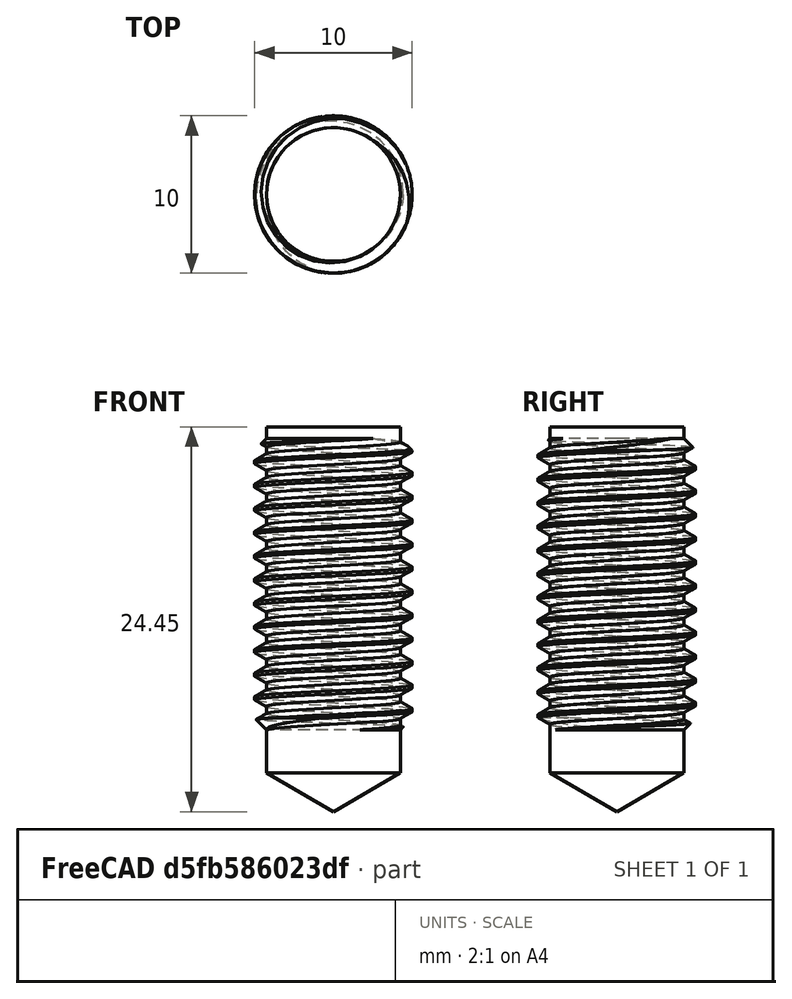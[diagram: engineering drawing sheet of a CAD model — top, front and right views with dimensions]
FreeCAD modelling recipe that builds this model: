
FCSTD DOCUMENT  (FreeCAD 0.22R36731 (Git))
Label: ThreadedHoll
License: All rights reserved
objects: Part::FeaturePython×1, Part::Cylinder×1, Part::Cone×1, Part::MultiFuse×1, Spreadsheet::Sheet×1, App::Part×1
note: 4 computed .brp shape members not serialized (recipe doc carries the construction recipe); baked Part::Feature solids carry a one-line shape summary decoded from their .brp

FEATURE [Part::FeaturePython] ThreadedRod  label="M10x20-ThreadedRod"  # Fasteners workbench fastener (typed FeaturePython)
  diameter = 10
  diameterCustom = 6
  invert = false
  leftHanded = false
  length = 20
  matchOuter = false
  offset = 0
  pitchCustom = 1
  thread = true
  type = 4
FEATURE [Part::Cylinder] Cylinder  label="円柱"
  Angle = 360
  AttacherType = Attacher::AttachEngine3D
  FirstAngle = 0
  Height = 22
  Placement = pos=(0,0,0) rot=(0,1,0;3.14159rad)
  Radius = 4.25
  SecondAngle = 0
  expr: Height = <<Spreadsheet>>.length * 1.1
  expr: Radius = Spreadsheet.Db / 2
FEATURE [Part::Cone] Cone  label="円錐"
  Angle = 360
  AttacherType = Attacher::AttachEngine3D
  Height = 2.45374
  Placement = pos=(0,0,-24.45) rot=(0,0,1;0rad)
  Radius1 = 0
  Radius2 = 4.25
  expr: Height = <<Spreadsheet>>.Db / 2 * tan(30)
  expr: Radius2 = <<Spreadsheet>>.Db / 2
FEATURE [Part::MultiFuse] Fusion  label="theadedHoll"
  Refine = true
  Shapes = -> [ThreadedRod,Cylinder,Cone]
FEATURE [Spreadsheet::Sheet] Spreadsheet
  cells = A1(size)='M10; B1(length)=20; C1(Db)=8.5; A2='M3; B2=2.5; A3='M4; B3=3.3; A4='M5; B4=4.2; A5='M6; B5=5; A6='M8; B6=6.8; A7='M10; B7=8.5; A8='M12; B8=10.2; A9='M14; B9=12; A10='M16; B10=14
FEATURE [App::Part] Part  label="ThreadHoll"
  Group = -> [Spreadsheet,Cylinder,Cone,ThreadedRod,Fusion]
  Origin = -> Origin
